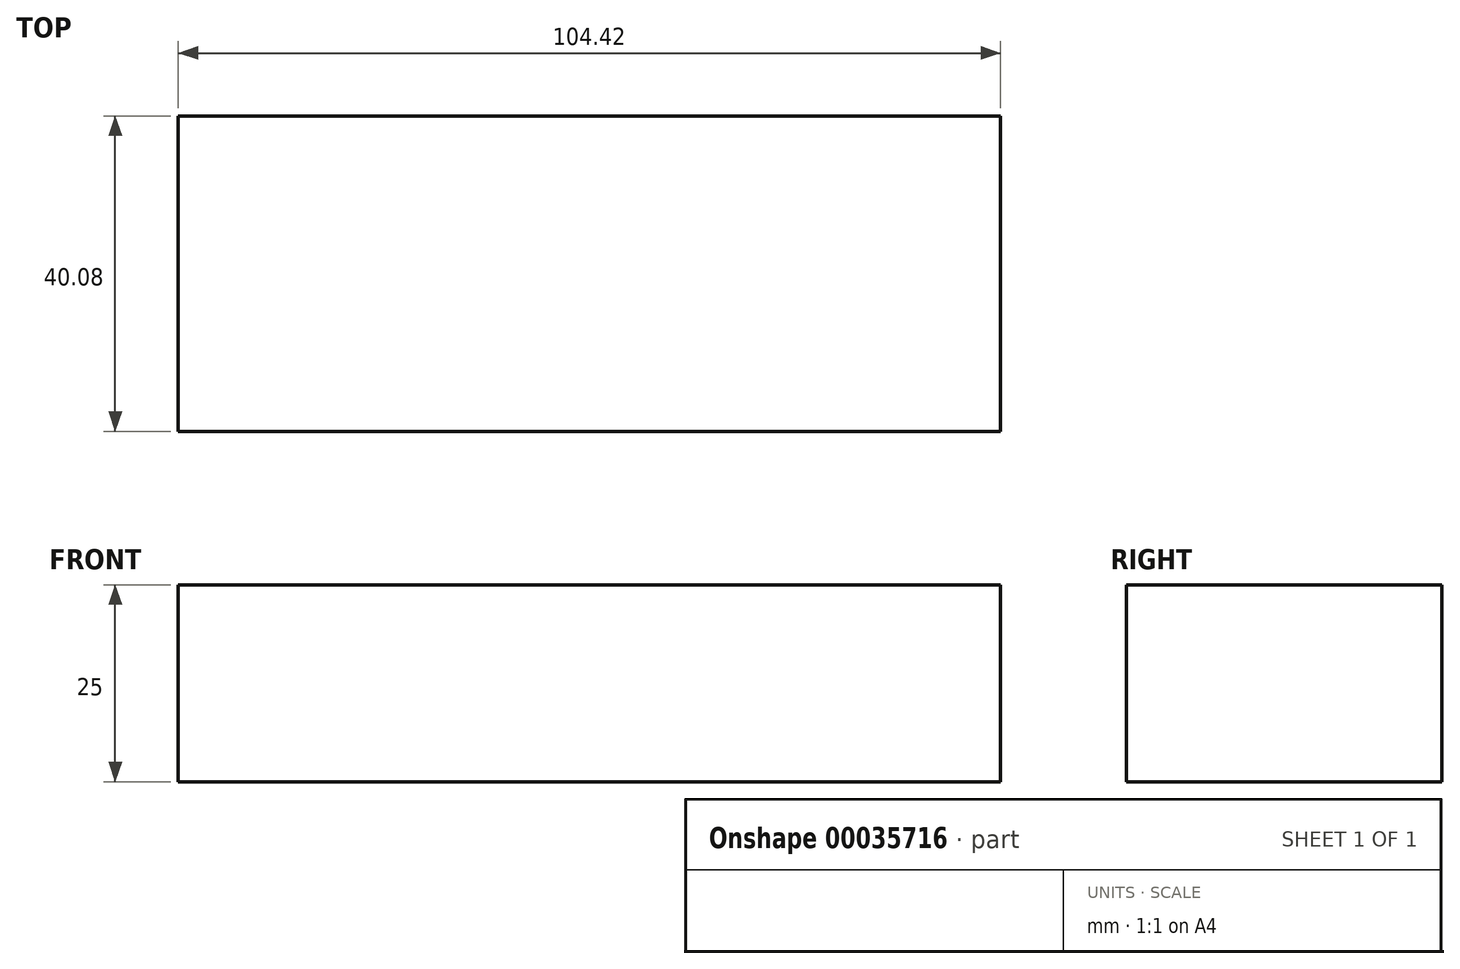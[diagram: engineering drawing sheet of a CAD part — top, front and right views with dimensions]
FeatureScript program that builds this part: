
annotation { "Feature Type Name" : "Feature", "Feature Type Description" : "" }
export const myFeature = defineFeature(function(context is Context, id is Id, definition is map)
    precondition{}
    {
        {
            var Q0;
            Q0=qCreatedBy(makeId("Top.planeOp"),FACE);
            var sketch = newSketch(context, id + "F0", { "sketchPlane" : qUnion([Q0])});
            skLineSegment(sketch, "E0.rect.bottom", {"start": v(52.2, 20.04) * mm, "end": v(-52.2, 20.04) * mm});
            skLineSegment(sketch, "E0.rect.top", {"start": v(52.2, -20.04) * mm, "end": v(-52.2, -20.04) * mm});
            skLineSegment(sketch, "E0.rect.left", {"start": v(52.2, 20.04) * mm, "end": v(52.2, -20.04) * mm});
            skLineSegment(sketch, "E0.rect.right", {"start": v(-52.2, 20.04) * mm, "end": v(-52.2, -20.04) * mm});
            skPoint(sketch, "E0.rect.middle", {"position": v(0, 0) * mm});
            skSolve(sketch);
        }
        {
            var Q0;
            Q0=makeQuery(id+"F0.imprint","IMPRINT",FACE,{"disambiguationData":[TD([[makeQuery(id+"F0.imprint","IMPRINT",EDGE,{"derivedFrom":sQuery(id+"F0.wireOp",EDGE,"E0.rect.bottom")}),1.0]])]});
            extrude(context, id + "F1", {"entities" : qUnion([Q0]), "depth" : 25 * mm, "hasDraft" : true, "draftAngle" : 0 * degree});
        }
    });
